# Revit family: PAV_ANAESTIVAC 2
name_source: partatom
category: Equipement de génie climatique
revit_build: Autodesk Revit 2018 (Build: 20170223_1515(x64)
units: mm (PartAtom-declared; Revit-internal decimal feet)

## family parameters
Basée sur le plan de construction = Non
Classification = Aucun
Cote de connecteur circulaire = Utiliser le diamètre
Couper avec des vides une fois chargée = Non
Partagée = Non
Point de calcul de pièce = Non
Toujours verticalement = Oui
Type d'élément = Normal

## types (4) — shared parameters
BRANCHEMENT_TERRE = Oui
COS_PHI = 0.9
DOUBLE_ALIMENTATION = Non
NEUTRE = Oui
PUISS_APPARENTE_2 = 0 VA
PUISS_ELECT_2 = 0 kW
Type_coffret = tableau éléctrique EPT : Coffret_PM2_3xSL150R
Zone de maintenance 1 = Oui
Zone de maintenance coffret = Oui
zero-valued in all types: HAUTEUR

## per-type parameters (varying)
- Y006V: ASPI_REFOULEMENT_VIDE_HAUT=38 mm  [stored 0.124672 ft]; ASPI_REFOULEMENT_VIDE_LARG=100 mm  [stored 0.328084 ft]; ASPI_REFOULEMENT_VIDE_LONG=181.5 mm; ASPI_REFOUL_LONGUEUR=181.5 mm; BOITE ELEC_HAUT=77 mm; DEBIT_ASPI_VIDE=75.0 m³/h; DEBIT_REFOUL_VIDE=75.0 m³/h; DESCR_ALIM_X=Alimentation électrique, 5G1mm²; DESCR_ASPI=Aspiration Vide; 75m3/h; G1"1/4"FEM; DESCR_REFOUL=Refoulement Vide; 75m3/h; G1"1/4"FEM; DIAM_ASPI_VIDE=32 mm  [stored 0.104987 ft]; DIAM_REFOUL_VIDE=32 mm  [stored 0.104987 ft]; ENSSEMBLE_LONGUEUR=195 mm; MOTEUR_DIAMETRE=154 mm  [stored 0.505249 ft]; NBR_POLES=3; NIVEAU_SONORE(dB(A))=58; POIDS(Kg)=13 mm; PUISS_APPARENTE=422 VA; PUISS_ELECT=0 kW; SOCLE_LARG=110 mm  [stored 0.360892 ft]; SOCLE_LONG=230 mm; SOCLE_PIECE_RAYON=80 mm  [stored 0.262467 ft]; SOCLE_TROU_DIAMETRE=11 mm  [stored 0.0360892 ft]; SOCLE_TROU_LARG=85 mm  [stored 0.278871 ft]; SOCLE_TROU_LONG=205 mm; TENSION_ALIM=400 V; VENT_DIAMETRE=250 mm; VENT_EPAISSEUR=61 mm  [stored 0.200131 ft]; VENT_HAUTEUR=130 mm  [stored 0.426509 ft]; VENT_RAYON_SUPPORT=125 mm  [stored 0.410105 ft]; VENT_RAYON_VIDE=90 mm
- Y011V: ASPI_REFOULEMENT_VIDE_HAUT=46 mm  [stored 0.150919 ft]; ASPI_REFOULEMENT_VIDE_LARG=115 mm  [stored 0.377297 ft]; ASPI_REFOULEMENT_VIDE_LONG=156 mm; ASPI_REFOUL_LONGUEUR=156 mm; BOITE ELEC_HAUT=80.5 mm  [stored 0.264108 ft]; DEBIT_ASPI_VIDE=144.0 m³/h; DEBIT_REFOUL_VIDE=144.0 m³/h; DESCR_ALIM_X=Alimentation électrique, 5G1.5mm²; DESCR_ASPI=Aspiration Vide; 144m3/h; G1"1/2"FEM; DESCR_REFOUL=Refoulement Vide; 144m3/h; G1"1/2"FEM; DIAM_ASPI_VIDE=40 mm  [stored 0.131234 ft]; DIAM_REFOUL_VIDE=40 mm  [stored 0.131234 ft]; ENSSEMBLE_LONGUEUR=186 mm; MOTEUR_DIAMETRE=161 mm; NBR_POLES=1; NIVEAU_SONORE(dB(A))=64; POIDS(Kg)=16 mm  [stored 0.0524934 ft]; PUISS_APPARENTE=1000 VA; PUISS_ELECT=1 kW; SOCLE_LARG=130 mm  [stored 0.426509 ft]; SOCLE_LONG=255 mm; SOCLE_PIECE_RAYON=95 mm; SOCLE_TROU_DIAMETRE=12 mm  [stored 0.0393701 ft]; SOCLE_TROU_LARG=95 mm; SOCLE_TROU_LONG=225 mm; TENSION_ALIM=400 V; VENT_DIAMETRE=286 mm; VENT_EPAISSEUR=75 mm; VENT_HAUTEUR=154 mm  [stored 0.505249 ft]; VENT_RAYON_SUPPORT=143 mm; VENT_RAYON_VIDE=108 mm  [stored 0.354331 ft]
- Y020V: ASPI_REFOULEMENT_VIDE_HAUT=48 mm  [stored 0.15748 ft]; ASPI_REFOULEMENT_VIDE_LARG=120 mm  [stored 0.393701 ft]; ASPI_REFOULEMENT_VIDE_LONG=218 mm; ASPI_REFOUL_LONGUEUR=218 mm; BOITE ELEC_HAUT=88.5 mm  [stored 0.290354 ft]; DEBIT_ASPI_VIDE=210.0 m³/h; DEBIT_REFOUL_VIDE=210.0 m³/h; DESCR_ALIM_X=Alimentation électrique, 5G1.5mm²; DESCR_ASPI=Aspiration Vide; 210m3/h; G2"FEM; DESCR_REFOUL=Refoulement Vide; 210m3/h; G2"FEM; DIAM_ASPI_VIDE=50 mm  [stored 0.164042 ft]; DIAM_REFOUL_VIDE=50 mm  [stored 0.164042 ft]; ENSSEMBLE_LONGUEUR=238 mm; MOTEUR_DIAMETRE=177 mm; NBR_POLES=3; NIVEAU_SONORE(dB(A))=68; POIDS(Kg)=23.5 mm  [stored 0.0770997 ft]; PUISS_APPARENTE=1667 VA; PUISS_ELECT=2 kW; SOCLE_LARG=155 mm  [stored 0.50853 ft]; SOCLE_LONG=295 mm; SOCLE_PIECE_RAYON=105 mm  [stored 0.344488 ft]; SOCLE_TROU_DIAMETRE=14 mm  [stored 0.0459318 ft]; SOCLE_TROU_LARG=115 mm  [stored 0.377297 ft]; SOCLE_TROU_LONG=260 mm; TENSION_ALIM=230 V; VENT_DIAMETRE=325 mm; VENT_EPAISSEUR=85 mm  [stored 0.278871 ft]; VENT_HAUTEUR=174 mm; VENT_RAYON_SUPPORT=162.5 mm; VENT_RAYON_VIDE=127.5 mm  [stored 0.418307 ft]
- Y030V: ASPI_REFOULEMENT_VIDE_HAUT=53 mm  [stored 0.173885 ft]; ASPI_REFOULEMENT_VIDE_LARG=125 mm  [stored 0.410105 ft]; ASPI_REFOULEMENT_VIDE_LONG=239 mm; ASPI_REFOUL_LONGUEUR=239 mm; BOITE ELEC_HAUT=103.5 mm  [stored 0.339567 ft]; DEBIT_ASPI_VIDE=306.0 m³/h; DEBIT_REFOUL_VIDE=306.0 m³/h; DESCR_ALIM_X=Alimentation électrique, 5G2.5mm²; DESCR_ASPI=Aspiration Vide; 306m3/h; G2"FEM; DESCR_REFOUL=Refoulement Vide; 306m3/h; G2"FEM; DIAM_ASPI_VIDE=50 mm  [stored 0.164042 ft]; DIAM_REFOUL_VIDE=50 mm  [stored 0.164042 ft]; ENSSEMBLE_LONGUEUR=269 mm; MOTEUR_DIAMETRE=207 mm; NBR_POLES=3; NIVEAU_SONORE(dB(A))=70; POIDS(Kg)=21 mm  [stored 0.0688976 ft]; PUISS_APPARENTE=2444 VA; PUISS_ELECT=2 kW; SOCLE_LARG=180 mm; SOCLE_LONG=325 mm; SOCLE_PIECE_RAYON=115 mm  [stored 0.377297 ft]; SOCLE_TROU_DIAMETRE=15 mm  [stored 0.0492126 ft]; SOCLE_TROU_LARG=140 mm  [stored 0.459318 ft]; SOCLE_TROU_LONG=290 mm; TENSION_ALIM=400 V; VENT_DIAMETRE=370 mm; VENT_EPAISSEUR=95 mm; VENT_HAUTEUR=197 mm; VENT_RAYON_SUPPORT=185 mm; VENT_RAYON_VIDE=150 mm

note: [stored X ft] marks values corroborated as IEEE doubles in the binary element streams (Revit-internal decimal feet)
